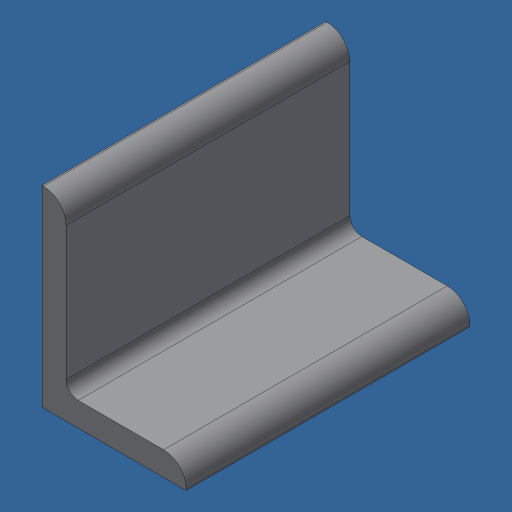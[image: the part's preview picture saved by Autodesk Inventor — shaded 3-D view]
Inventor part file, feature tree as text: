
AUTODESK INVENTOR PART (.ipt)
format: ipt  version: 2024.3 (Build 283343000, 343)  size: 136,192 bytes
history: native  units: mm (DEFAULTED — no unit token found)
features: other x1, extrude x1
ambient origin geometry x8: Origin, YZ Plane, XZ Plane, XY Plane, X Axis, Y Axis, Z Axis, Center Point
bodies: Body1 (feature_tree)
feature tree (2):
  other  "Finish - None"
  extrude  "6" X 8" X 1""  Depth=25.4mm
